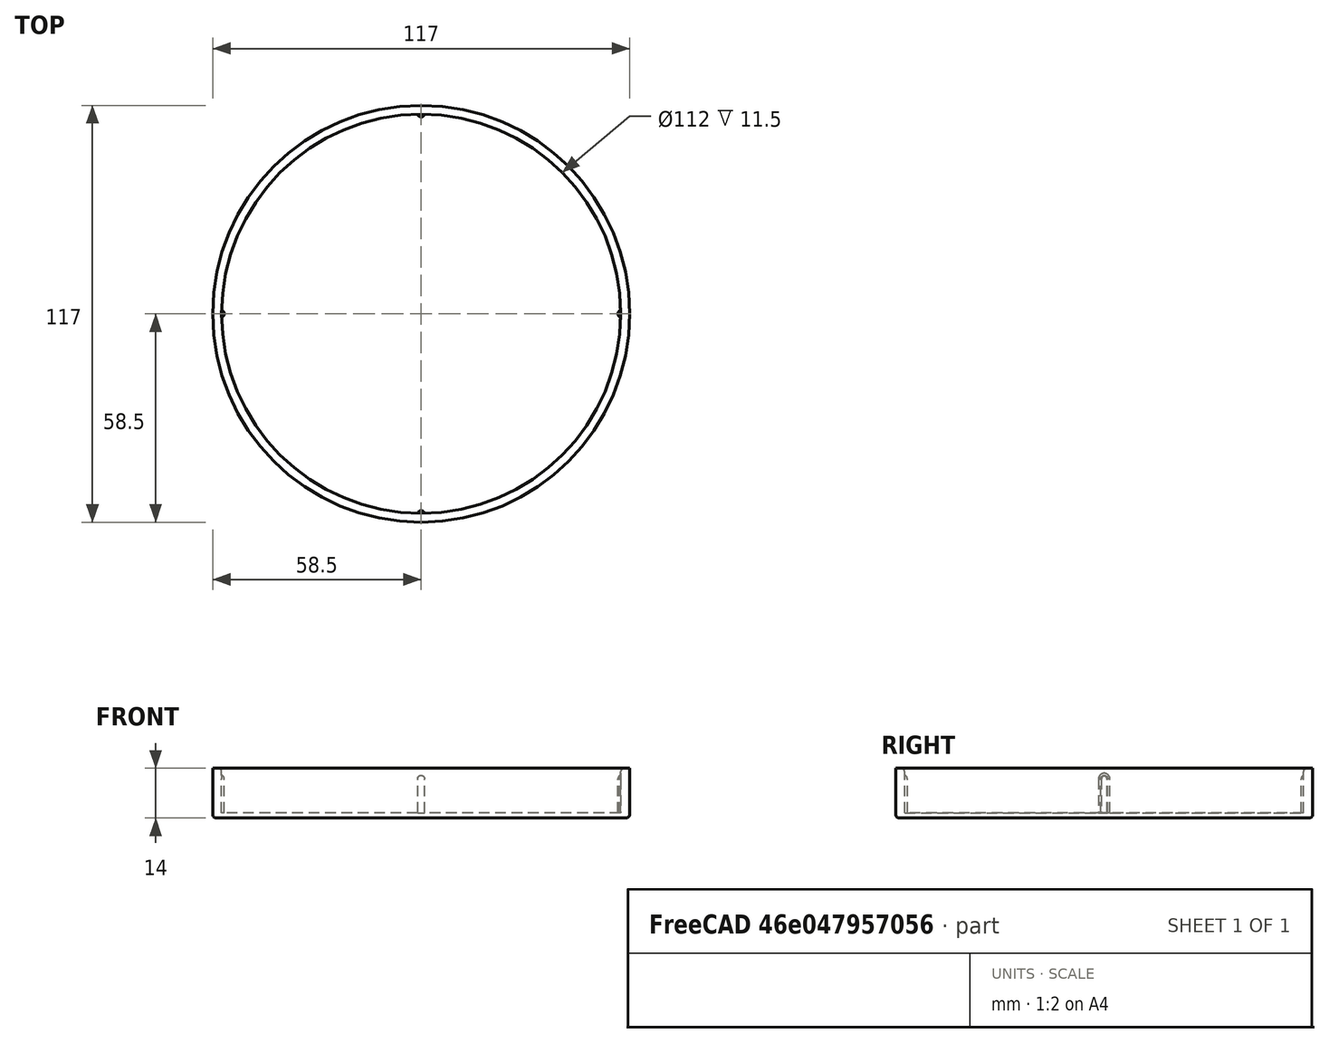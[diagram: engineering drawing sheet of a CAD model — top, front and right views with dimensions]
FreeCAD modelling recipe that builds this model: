
FCSTD DOCUMENT  (FreeCAD 0.15R4671 (Git))
Label: hartblei-500mm-lens-cap
License: All rights reserved
LicenseURL: http://en.wikipedia.org/wiki/All_rights_reserved
objects: Part::Cylinder×6, Part::Fillet×6, Part::Cut×1, Part::MultiFuse×1
note: 14 computed .brp shape members not serialized (recipe doc carries the construction recipe); baked Part::Feature solids carry a one-line shape summary decoded from their .brp

FEATURE [Part::Cylinder] Cylinder
  Angle = 360
  Height = 15
  Placement = pos=(0,0,1.5) rot=(0,0,1;0rad)
  Radius = 56
FEATURE [Part::Cylinder] Cylinder001
  Angle = 360
  Height = 14
  Radius = 58.5
FEATURE [Part::Cut] Cut
  Base = -> Cylinder001
  Tool = -> Cylinder
FEATURE [Part::Cylinder] Cylinder002
  Angle = 360
  Height = 12
  Radius = 1
FEATURE [Part::Fillet] Fillet001
  Base = -> Cylinder002
  Edges = 1 edges r=1: [Edge1]
  Placement = pos=(-56.25,0,0) rot=(0,0,1;0rad)
FEATURE [Part::Cylinder] Cylinder003
  Angle = 360
  Height = 12
  Radius = 1
FEATURE [Part::Fillet] Fillet002
  Base = -> Cylinder003
  Edges = 1 edges r=1: [Edge1]
  Placement = pos=(56.24,0,0) rot=(0,0,1;0rad)
FEATURE [Part::Cylinder] Cylinder004
  Angle = 360
  Height = 12
  Radius = 1
FEATURE [Part::Fillet] Fillet003
  Base = -> Cylinder004
  Edges = 1 edges r=1: [Edge1]
  Placement = pos=(0,-56.25,0) rot=(0,0,1;0rad)
FEATURE [Part::Cylinder] Cylinder005
  Angle = 360
  Height = 12
  Radius = 1
FEATURE [Part::Fillet] Fillet004
  Base = -> Cylinder005
  Edges = 1 edges r=1: [Edge1]
  Placement = pos=(0,56.25,0) rot=(0,0,1;0rad)
FEATURE [Part::Fillet] Fillet
  Base = -> Cut
  Edges = 1 edges r=1: [Edge4]
FEATURE [Part::MultiFuse] Fusion
  Shapes = -> [Fillet,Fillet002,Fillet004,Fillet001,Fillet003]
FEATURE [Part::Fillet] Fillet005
  Base = -> Fusion
  Edges = 2 edges r=1: [Edge6,Edge16]
